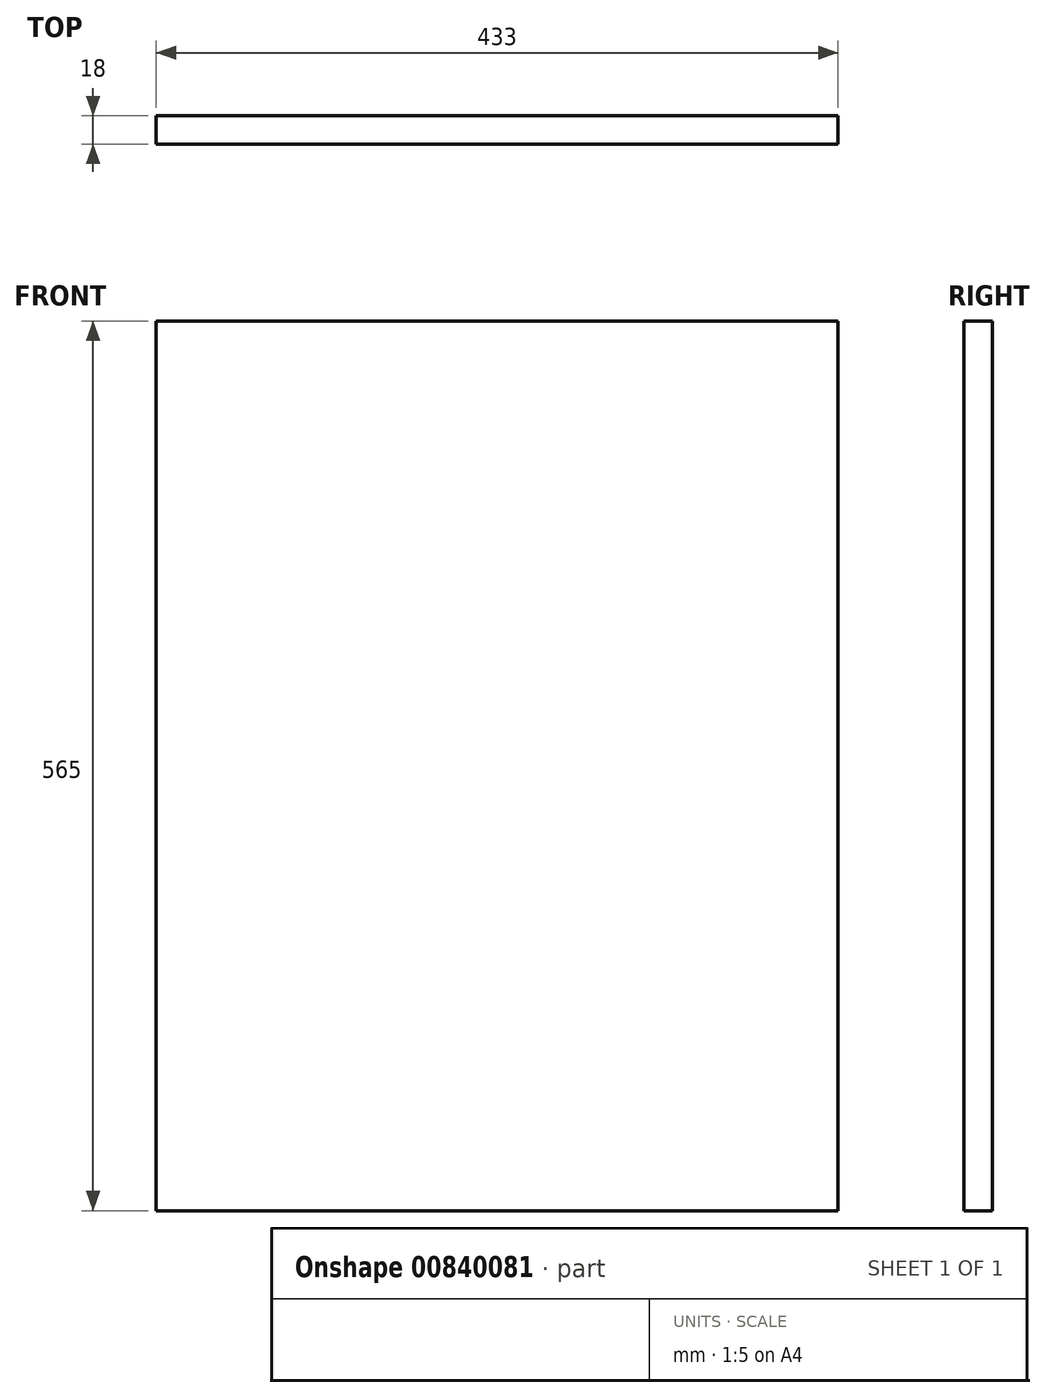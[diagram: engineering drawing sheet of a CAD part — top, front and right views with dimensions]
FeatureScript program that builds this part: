
annotation { "Feature Type Name" : "Feature", "Feature Type Description" : "" }
export const myFeature = defineFeature(function(context is Context, id is Id, definition is map)
    precondition{}
    {
        {
            var Q0;
            Q0=qCreatedBy(makeId("Front.planeOp"),FACE);
            var sketch = newSketch(context, id + "F0", { "sketchPlane" : qUnion([Q0])});
            skLineSegment(sketch, "E0.bottom", {"start": v(-244.75, 371.48) * mm, "end": v(188.25, 371.48) * mm});
            skLineSegment(sketch, "E0.top", {"start": v(-244.75, -193.52) * mm, "end": v(188.25, -193.52) * mm});
            skLineSegment(sketch, "E0.left", {"start": v(-244.75, 371.48) * mm, "end": v(-244.75, -193.52) * mm});
            skLineSegment(sketch, "E0.right", {"start": v(188.25, 371.48) * mm, "end": v(188.25, -193.52) * mm});
            skSolve(sketch);
        }
        {
            var Q0;
            Q0=qSketchRegion(id+"F0",true);
            extrude(context, id + "F1", {"entities" : qUnion([Q0]), "oppositeDirection" : true, "depth" : 18 * mm, "offsetDistance" : 25 * mm});
        }
    });
